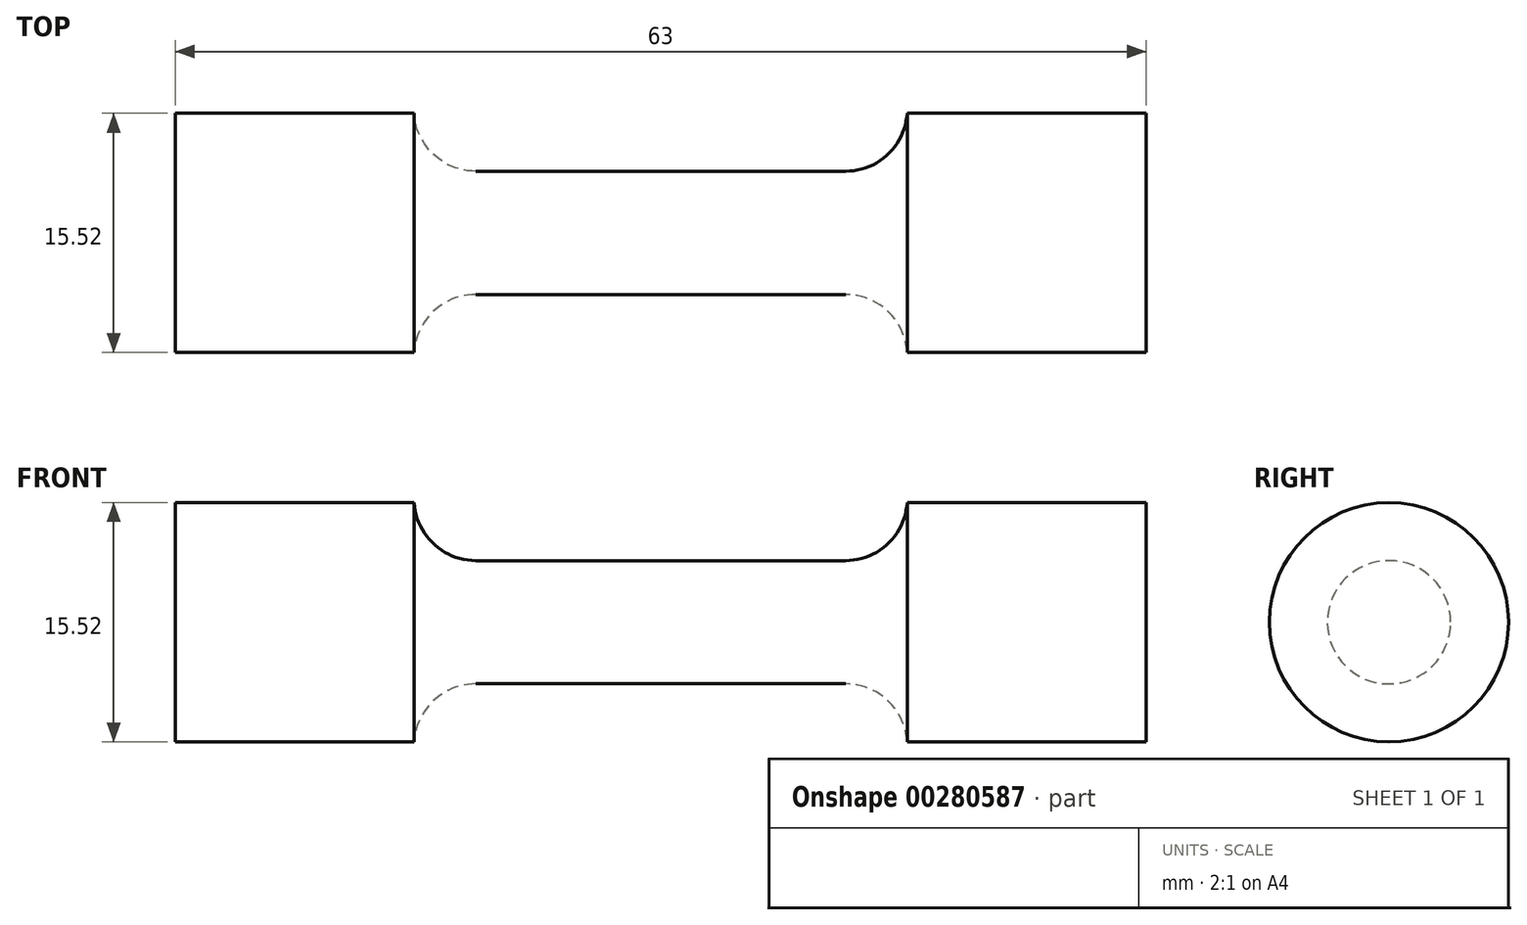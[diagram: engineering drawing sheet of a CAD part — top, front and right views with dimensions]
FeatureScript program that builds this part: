
annotation { "Feature Type Name" : "Feature", "Feature Type Description" : "" }
export const myFeature = defineFeature(function(context is Context, id is Id, definition is map)
    precondition{}
    {
        {
            var Q0;
            Q0=qCreatedBy(makeId("Front.planeOp"),FACE);
            var sketch = newSketch(context, id + "F0", { "sketchPlane" : qUnion([Q0])});
            skLineSegment(sketch, "E0", {"start": v(0, 4) * mm, "end": v(12, 4) * mm});
            skArc(sketch, "E1", {"start": v(12, 4) * mm, "mid": v(14.74, 5.09) * mm, "end": v(16, 7.76) * mm});
            skLineSegment(sketch, "E2", {"start": v(16, 7.76) * mm, "end": v(31.5, 7.76) * mm});
            skLineSegment(sketch, "E3", {"start": v(31.5, 7.76) * mm, "end": v(31.5, 0) * mm});
            skLineSegment(sketch, "E4.MirrorCS", {"start": v(0, 4) * mm, "end": v(-12, 4) * mm});
            skLineSegment(sketch, "E5.MirrorCS", {"start": v(-31.5, 7.76) * mm, "end": v(-31.5, 0) * mm});
            skLineSegment(sketch, "E6.MirrorCS", {"start": v(-16, 7.76) * mm, "end": v(-31.5, 7.76) * mm});
            skArc(sketch, "E7.MirrorCS", {"start": v(-12, 4) * mm, "mid": v(-14.74, 5.09) * mm, "end": v(-16, 7.76) * mm});
            skLineSegment(sketch, "E8", {"start": v(-31.5, 0) * mm, "end": v(31.5, 0) * mm});
            skSolve(sketch);
        }
        {
            var Q0;
            Q0 = qSketchRegion(id + "F0", true);
            var Q1;
            Q1=sQuery(id+"F0.wireOp",EDGE,"E8");
            revolve(context, id + "F1", {"entities" : qUnion([Q0]), "axis" : qUnion([Q1]), "revolveType" : RevolveType.FULL});
        }
    });
